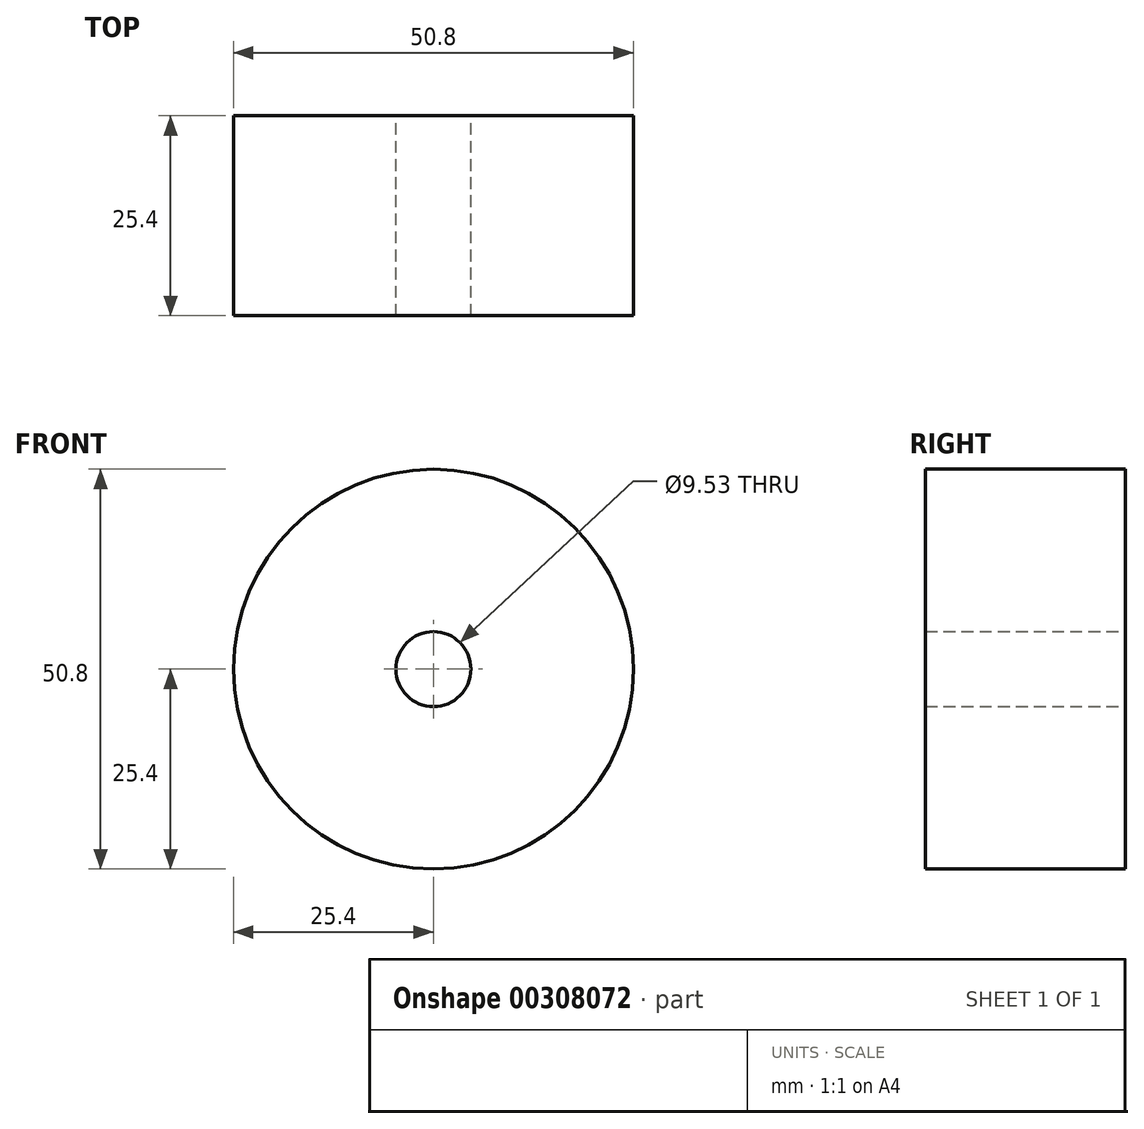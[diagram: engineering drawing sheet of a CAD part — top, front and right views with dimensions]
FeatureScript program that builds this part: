
annotation { "Feature Type Name" : "Feature", "Feature Type Description" : "" }
export const myFeature = defineFeature(function(context is Context, id is Id, definition is map)
    precondition{}
    {
        {
            var Q0;
            Q0=qCreatedBy(makeId("Front.planeOp"),FACE);
            var sketch = newSketch(context, id + "F0", { "sketchPlane" : qUnion([Q0])});
            skCircle(sketch, "E0", {"center": v(0, 0) * mm, "radius": 25.4 * mm});
            skCircle(sketch, "E1", {"center": v(0, 0) * mm, "radius": 4.76 * mm});
            skSolve(sketch);
        }
        {
            var Q0;
            Q0 = qSketchRegion(id + "F0", true);
            extrude(context, id + "F1", {"entities" : qUnion([Q0]), "depth" : 25.4 * mm, "offsetDistance" : 25.4 * mm});
        }
    });
